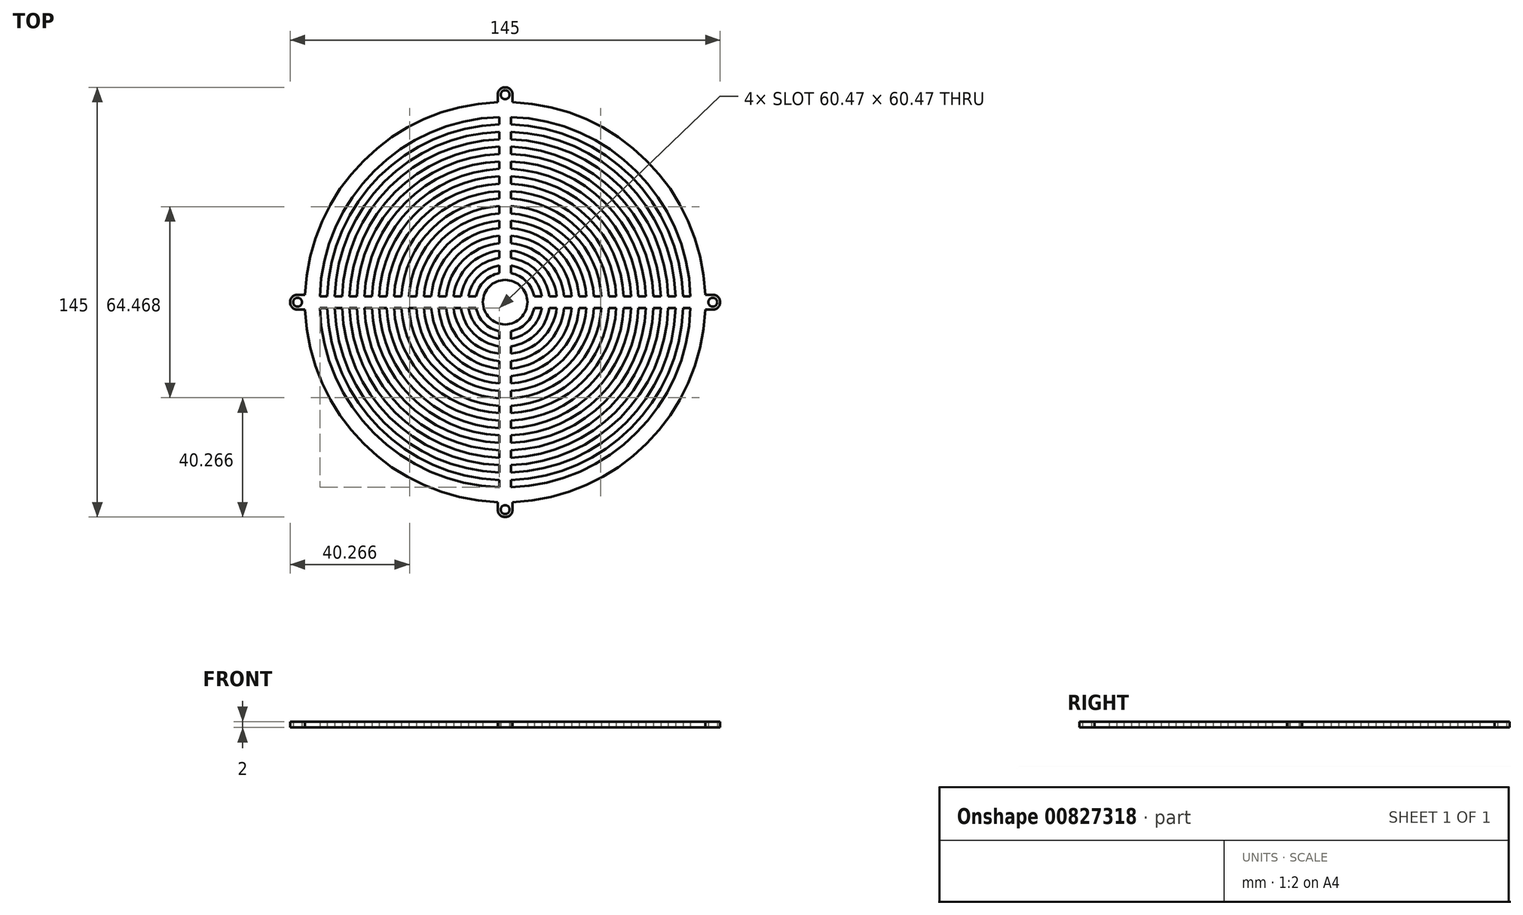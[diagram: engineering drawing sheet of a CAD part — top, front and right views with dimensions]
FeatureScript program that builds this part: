
annotation { "Feature Type Name" : "Feature", "Feature Type Description" : "" }
export const myFeature = defineFeature(function(context is Context, id is Id, definition is map)
    precondition{}
    {
        {
            var Q0;
            Q0=qCreatedBy(makeId("Top.planeOp"),FACE);
            var sketch = newSketch(context, id + "F0", { "sketchPlane" : qUnion([Q0])});
            skArc(sketch, "E0", {"start": v(-62.47, -2) * mm, "mid": v(-44.2, -44.2) * mm, "end": v(-2, -62.47) * mm});
            skArc(sketch, "E1", {"start": v(-2.5, 67.45) * mm, "mid": v(-47.73, 47.73) * mm, "end": v(-67.45, 2.5) * mm});
            skArc(sketch, "E2", {"start": v(-59.97, -2) * mm, "mid": v(-42.43, -42.43) * mm, "end": v(-2, -59.97) * mm});
            skArc(sketch, "E3", {"start": v(-57.47, -2) * mm, "mid": v(-40.66, -40.66) * mm, "end": v(-2, -57.47) * mm});
            skArc(sketch, "E4", {"start": v(-54.96, -2) * mm, "mid": v(-38.9, -38.9) * mm, "end": v(-2, -54.96) * mm});
            skArc(sketch, "E5", {"start": v(-52.46, -2) * mm, "mid": v(-37.12, -37.12) * mm, "end": v(-2, -52.46) * mm});
            skArc(sketch, "E6", {"start": v(-49.96, -2) * mm, "mid": v(-35.36, -35.36) * mm, "end": v(-2, -49.96) * mm});
            skArc(sketch, "E7", {"start": v(-47.46, -2) * mm, "mid": v(-33.59, -33.59) * mm, "end": v(-2, -47.46) * mm});
            skArc(sketch, "E8", {"start": v(-44.96, -2) * mm, "mid": v(-31.82, -31.82) * mm, "end": v(-2, -44.96) * mm});
            skArc(sketch, "E9", {"start": v(-42.45, -2) * mm, "mid": v(-30.05, -30.05) * mm, "end": v(-2, -42.45) * mm});
            skArc(sketch, "E10", {"start": v(-37.45, -2) * mm, "mid": v(-26.52, -26.52) * mm, "end": v(-2, -37.45) * mm});
            skArc(sketch, "E11", {"start": v(-39.95, -2) * mm, "mid": v(-28.28, -28.28) * mm, "end": v(-2, -39.95) * mm});
            skArc(sketch, "E12", {"start": v(-32.44, -2) * mm, "mid": v(-22.98, -22.98) * mm, "end": v(-2, -32.44) * mm});
            skArc(sketch, "E13", {"start": v(-34.94, -2) * mm, "mid": v(-24.75, -24.75) * mm, "end": v(-2, -34.94) * mm});
            skArc(sketch, "E14", {"start": v(-29.93, -2) * mm, "mid": v(-21.21, -21.21) * mm, "end": v(-2, -29.93) * mm});
            skArc(sketch, "E15", {"start": v(-27.43, -2) * mm, "mid": v(-19.45, -19.45) * mm, "end": v(-2, -27.43) * mm});
            skArc(sketch, "E16", {"start": v(-22.41, -2) * mm, "mid": v(-15.9, -15.9) * mm, "end": v(-2, -22.41) * mm});
            skArc(sketch, "E17", {"start": v(-19.9, -2) * mm, "mid": v(-14.14, -14.14) * mm, "end": v(-2, -19.9) * mm});
            skArc(sketch, "E18", {"start": v(-17.39, -2) * mm, "mid": v(-12.37, -12.37) * mm, "end": v(-2, -17.39) * mm});
            skArc(sketch, "E19", {"start": v(-9.8, -2) * mm, "mid": v(-7.07, -7.07) * mm, "end": v(-2, -9.8) * mm});
            skArc(sketch, "E20", {"start": v(-12.34, -2) * mm, "mid": v(-8.84, -8.84) * mm, "end": v(-2, -12.34) * mm});
            skArc(sketch, "E21", {"start": v(-14.87, -2) * mm, "mid": v(-10.6, -10.6) * mm, "end": v(-2, -14.87) * mm});
            skArc(sketch, "E22", {"start": v(-24.92, -2) * mm, "mid": v(-17.68, -17.68) * mm, "end": v(-2, -24.92) * mm});
            skLineSegment(sketch, "E23", {"start": v(-2, 62.47) * mm, "end": v(-2, 59.97) * mm});
            skLineSegment(sketch, "E24", {"start": v(2, 62.47) * mm, "end": v(2, 59.97) * mm});
            skLineSegment(sketch, "E25", {"start": v(-62.47, -2) * mm, "end": v(-59.97, -2) * mm});
            skLineSegment(sketch, "E26", {"start": v(-62.47, 2) * mm, "end": v(-59.97, 2) * mm});
            skLineSegment(sketch, "E27.trimOffspring", {"start": v(-57.47, 2) * mm, "end": v(-54.96, 2) * mm});
            skLineSegment(sketch, "E28.trimOffspring", {"start": v(-52.46, 2) * mm, "end": v(-49.96, 2) * mm});
            skLineSegment(sketch, "E29.trimOffspring", {"start": v(-57.47, -2) * mm, "end": v(-54.96, -2) * mm});
            skLineSegment(sketch, "E30.trimOffspring", {"start": v(-52.46, -2) * mm, "end": v(-49.96, -2) * mm});
            skLineSegment(sketch, "E31.trimOffspring", {"start": v(-47.46, -2) * mm, "end": v(-44.96, -2) * mm});
            skLineSegment(sketch, "E32.trimOffspring", {"start": v(-47.46, 2) * mm, "end": v(-44.96, 2) * mm});
            skLineSegment(sketch, "E33.trimOffspring", {"start": v(-42.45, 2) * mm, "end": v(-39.95, 2) * mm});
            skLineSegment(sketch, "E34.trimOffspring", {"start": v(-42.45, -2) * mm, "end": v(-39.95, -2) * mm});
            skLineSegment(sketch, "E35.trimOffspring", {"start": v(-37.45, 2) * mm, "end": v(-34.94, 2) * mm});
            skLineSegment(sketch, "E36.trimOffspring", {"start": v(-37.45, -2) * mm, "end": v(-34.94, -2) * mm});
            skLineSegment(sketch, "E37.trimOffspring", {"start": v(-32.44, 2) * mm, "end": v(-29.93, 2) * mm});
            skLineSegment(sketch, "E38.trimOffspring", {"start": v(-32.44, -2) * mm, "end": v(-29.93, -2) * mm});
            skLineSegment(sketch, "E39.trimOffspring", {"start": v(-27.43, 2) * mm, "end": v(-24.92, 2) * mm});
            skLineSegment(sketch, "E40.trimOffspring", {"start": v(-27.43, -2) * mm, "end": v(-24.92, -2) * mm});
            skLineSegment(sketch, "E41.trimOffspring", {"start": v(-22.41, 2) * mm, "end": v(-19.9, 2) * mm});
            skLineSegment(sketch, "E42.trimOffspring", {"start": v(-22.41, -2) * mm, "end": v(-19.9, -2) * mm});
            skLineSegment(sketch, "E43.trimOffspring", {"start": v(-17.39, 2) * mm, "end": v(-14.87, 2) * mm});
            skLineSegment(sketch, "E44.trimOffspring", {"start": v(-17.39, -2) * mm, "end": v(-14.87, -2) * mm});
            skLineSegment(sketch, "E45.trimOffspring", {"start": v(-12.34, 2) * mm, "end": v(-9.8, 2) * mm});
            skLineSegment(sketch, "E46.trimOffspring", {"start": v(-12.34, -2) * mm, "end": v(-9.8, -2) * mm});
            skLineSegment(sketch, "E47.trimOffspring", {"start": v(-2, -9.8) * mm, "end": v(-2, -12.34) * mm});
            skLineSegment(sketch, "E48.trimOffspring", {"start": v(2, -9.8) * mm, "end": v(2, -12.34) * mm});
            skLineSegment(sketch, "E49.trimOffspring", {"start": v(-2, 12.34) * mm, "end": v(-2, 9.8) * mm});
            skLineSegment(sketch, "E50.trimOffspring", {"start": v(2, 12.34) * mm, "end": v(2, 9.8) * mm});
            skLineSegment(sketch, "E51.trimOffspring", {"start": v(2, 17.39) * mm, "end": v(2, 14.87) * mm});
            skLineSegment(sketch, "E52.trimOffspring", {"start": v(-2, 17.39) * mm, "end": v(-2, 14.87) * mm});
            skArc(sketch, "E53.trimOffspring", {"start": v(-2, 12.34) * mm, "mid": v(-8.84, 8.84) * mm, "end": v(-12.34, 2) * mm});
            skArc(sketch, "E54.trimOffspring", {"start": v(-2, 9.8) * mm, "mid": v(-7.07, 7.07) * mm, "end": v(-9.8, 2) * mm});
            skArc(sketch, "E55.trimOffspring", {"start": v(-2, 14.87) * mm, "mid": v(-10.6, 10.6) * mm, "end": v(-14.87, 2) * mm});
            skArc(sketch, "E56.trimOffspring", {"start": v(-2, 17.39) * mm, "mid": v(-12.37, 12.37) * mm, "end": v(-17.39, 2) * mm});
            skArc(sketch, "E57.trimOffspring", {"start": v(-2, 19.9) * mm, "mid": v(-14.14, 14.14) * mm, "end": v(-19.9, 2) * mm});
            skArc(sketch, "E58.trimOffspring", {"start": v(-2, 22.41) * mm, "mid": v(-15.9, 15.9) * mm, "end": v(-22.41, 2) * mm});
            skArc(sketch, "E59.trimOffspring", {"start": v(-2, 24.92) * mm, "mid": v(-17.68, 17.68) * mm, "end": v(-24.92, 2) * mm});
            skArc(sketch, "E60.trimOffspring", {"start": v(-2, 27.43) * mm, "mid": v(-19.45, 19.45) * mm, "end": v(-27.43, 2) * mm});
            skArc(sketch, "E61.trimOffspring", {"start": v(-2, 29.93) * mm, "mid": v(-21.21, 21.21) * mm, "end": v(-29.93, 2) * mm});
            skArc(sketch, "E62.trimOffspring", {"start": v(-2, 32.44) * mm, "mid": v(-22.98, 22.98) * mm, "end": v(-32.44, 2) * mm});
            skLineSegment(sketch, "E63.trimOffspring", {"start": v(-2, 22.41) * mm, "end": v(-2, 19.9) * mm});
            skLineSegment(sketch, "E64.trimOffspring", {"start": v(2, 22.41) * mm, "end": v(2, 19.9) * mm});
            skLineSegment(sketch, "E65.trimOffspring", {"start": v(2, 27.43) * mm, "end": v(2, 24.92) * mm});
            skLineSegment(sketch, "E66.trimOffspring", {"start": v(-2, 27.43) * mm, "end": v(-2, 24.92) * mm});
            skLineSegment(sketch, "E67.trimOffspring", {"start": v(-2, 32.44) * mm, "end": v(-2, 29.93) * mm});
            skLineSegment(sketch, "E68.trimOffspring", {"start": v(2, 32.44) * mm, "end": v(2, 29.93) * mm});
            skArc(sketch, "E69.trimOffspring", {"start": v(-2, 34.94) * mm, "mid": v(-24.75, 24.75) * mm, "end": v(-34.94, 2) * mm});
            skArc(sketch, "E70.trimOffspring", {"start": v(-2, 37.45) * mm, "mid": v(-26.52, 26.52) * mm, "end": v(-37.45, 2) * mm});
            skArc(sketch, "E71.trimOffspring", {"start": v(-2, 39.95) * mm, "mid": v(-28.28, 28.28) * mm, "end": v(-39.95, 2) * mm});
            skArc(sketch, "E72.trimOffspring", {"start": v(-2, 42.45) * mm, "mid": v(-30.05, 30.05) * mm, "end": v(-42.45, 2) * mm});
            skArc(sketch, "E73.trimOffspring", {"start": v(-2, 44.96) * mm, "mid": v(-31.82, 31.82) * mm, "end": v(-44.96, 2) * mm});
            skArc(sketch, "E74.trimOffspring", {"start": v(-2, 47.46) * mm, "mid": v(-33.59, 33.59) * mm, "end": v(-47.46, 2) * mm});
            skLineSegment(sketch, "E75.trimOffspring", {"start": v(-2, 37.45) * mm, "end": v(-2, 34.94) * mm});
            skLineSegment(sketch, "E76.trimOffspring", {"start": v(2, 37.45) * mm, "end": v(2, 34.94) * mm});
            skLineSegment(sketch, "E77.trimOffspring", {"start": v(2, 42.45) * mm, "end": v(2, 39.95) * mm});
            skLineSegment(sketch, "E78.trimOffspring", {"start": v(-2, 42.45) * mm, "end": v(-2, 39.95) * mm});
            skLineSegment(sketch, "E79.trimOffspring", {"start": v(-2, 47.46) * mm, "end": v(-2, 44.96) * mm});
            skArc(sketch, "E80.trimOffspring", {"start": v(-2, 49.96) * mm, "mid": v(-35.36, 35.36) * mm, "end": v(-49.96, 2) * mm});
            skLineSegment(sketch, "E81.trimOffspring", {"start": v(2, 47.46) * mm, "end": v(2, 44.96) * mm});
            skArc(sketch, "E82.trimOffspring", {"start": v(-2, 52.46) * mm, "mid": v(-37.12, 37.12) * mm, "end": v(-52.46, 2) * mm});
            skArc(sketch, "E83.trimOffspring", {"start": v(-2, 54.96) * mm, "mid": v(-38.9, 38.9) * mm, "end": v(-54.96, 2) * mm});
            skArc(sketch, "E84.trimOffspring", {"start": v(-2, 57.47) * mm, "mid": v(-40.66, 40.66) * mm, "end": v(-57.47, 2) * mm});
            skArc(sketch, "E85.trimOffspring", {"start": v(-2, 59.97) * mm, "mid": v(-42.43, 42.43) * mm, "end": v(-59.97, 2) * mm});
            skLineSegment(sketch, "E86.trimOffspring", {"start": v(-2, 52.46) * mm, "end": v(-2, 49.96) * mm});
            skLineSegment(sketch, "E87.trimOffspring", {"start": v(2, 52.46) * mm, "end": v(2, 49.96) * mm});
            skLineSegment(sketch, "E88.trimOffspring", {"start": v(2, 57.47) * mm, "end": v(2, 54.96) * mm});
            skLineSegment(sketch, "E89.trimOffspring", {"start": v(-2, 57.47) * mm, "end": v(-2, 54.96) * mm});
            skArc(sketch, "E90.trimOffspring", {"start": v(-2, 62.47) * mm, "mid": v(-44.2, 44.2) * mm, "end": v(-62.47, 2) * mm});
            skArc(sketch, "E91.trimOffspring", {"start": v(2, -9.8) * mm, "mid": v(7.07, -7.07) * mm, "end": v(9.8, -2) * mm});
            skArc(sketch, "E92.trimOffspring", {"start": v(2, -12.34) * mm, "mid": v(8.84, -8.84) * mm, "end": v(12.34, -2) * mm});
            skArc(sketch, "E93.trimOffspring", {"start": v(2, -14.87) * mm, "mid": v(10.6, -10.6) * mm, "end": v(14.87, -2) * mm});
            skArc(sketch, "E94.trimOffspring", {"start": v(2, -17.39) * mm, "mid": v(12.37, -12.37) * mm, "end": v(17.39, -2) * mm});
            skArc(sketch, "E95.trimOffspring", {"start": v(2, -19.9) * mm, "mid": v(14.14, -14.14) * mm, "end": v(19.9, -2) * mm});
            skArc(sketch, "E96.trimOffspring", {"start": v(2, -22.41) * mm, "mid": v(15.9, -15.9) * mm, "end": v(22.41, -2) * mm});
            skArc(sketch, "E97.trimOffspring", {"start": v(2, -24.92) * mm, "mid": v(17.68, -17.68) * mm, "end": v(24.92, -2) * mm});
            skArc(sketch, "E98.trimOffspring", {"start": v(2, -27.43) * mm, "mid": v(19.45, -19.45) * mm, "end": v(27.43, -2) * mm});
            skArc(sketch, "E99.trimOffspring", {"start": v(2, -29.93) * mm, "mid": v(21.21, -21.21) * mm, "end": v(29.93, -2) * mm});
            skArc(sketch, "E100.trimOffspring", {"start": v(2, -32.44) * mm, "mid": v(22.98, -22.98) * mm, "end": v(32.44, -2) * mm});
            skArc(sketch, "E101.trimOffspring", {"start": v(2, -34.94) * mm, "mid": v(24.75, -24.75) * mm, "end": v(34.94, -2) * mm});
            skArc(sketch, "E102.trimOffspring", {"start": v(2, -37.45) * mm, "mid": v(26.52, -26.52) * mm, "end": v(37.45, -2) * mm});
            skArc(sketch, "E103.trimOffspring", {"start": v(2, -39.95) * mm, "mid": v(28.28, -28.28) * mm, "end": v(39.95, -2) * mm});
            skArc(sketch, "E104.trimOffspring", {"start": v(2, -42.45) * mm, "mid": v(30.05, -30.05) * mm, "end": v(42.45, -2) * mm});
            skLineSegment(sketch, "E105.trimOffspring", {"start": v(-2, -14.87) * mm, "end": v(-2, -17.39) * mm});
            skLineSegment(sketch, "E106.trimOffspring", {"start": v(-2, -19.9) * mm, "end": v(-2, -22.41) * mm});
            skLineSegment(sketch, "E107.trimOffspring", {"start": v(2, -19.9) * mm, "end": v(2, -22.41) * mm});
            skLineSegment(sketch, "E108", {"start": v(2, -14.87) * mm, "end": v(2, -17.39) * mm});
            skLineSegment(sketch, "E109.trimOffspring", {"start": v(2, -29.93) * mm, "end": v(2, -32.44) * mm});
            skLineSegment(sketch, "E110.trimOffspring", {"start": v(-2, -29.93) * mm, "end": v(-2, -32.44) * mm});
            skLineSegment(sketch, "E111", {"start": v(2, -27.43) * mm, "end": v(2, -24.92) * mm});
            skLineSegment(sketch, "E112", {"start": v(-2, -27.43) * mm, "end": v(-2, -24.92) * mm});
            skLineSegment(sketch, "E113.trimOffspring", {"start": v(-2, -34.94) * mm, "end": v(-2, -37.45) * mm});
            skLineSegment(sketch, "E114.trimOffspring", {"start": v(-2, -39.95) * mm, "end": v(-2, -42.45) * mm});
            skLineSegment(sketch, "E115.trimOffspring", {"start": v(2, -39.95) * mm, "end": v(2, -42.45) * mm});
            skLineSegment(sketch, "E116.trimOffspring", {"start": v(-2, -44.96) * mm, "end": v(-2, -47.46) * mm});
            skArc(sketch, "E117.trimOffspring", {"start": v(2, -44.96) * mm, "mid": v(31.82, -31.82) * mm, "end": v(44.96, -2) * mm});
            skArc(sketch, "E118.trimOffspring", {"start": v(2, -47.46) * mm, "mid": v(33.59, -33.59) * mm, "end": v(47.46, -2) * mm});
            skArc(sketch, "E119.trimOffspring", {"start": v(2, -49.96) * mm, "mid": v(35.36, -35.36) * mm, "end": v(49.96, -2) * mm});
            skArc(sketch, "E120.trimOffspring", {"start": v(2, -52.46) * mm, "mid": v(37.12, -37.12) * mm, "end": v(52.46, -2) * mm});
            skArc(sketch, "E121.trimOffspring", {"start": v(2, -57.47) * mm, "mid": v(40.66, -40.66) * mm, "end": v(57.47, -2) * mm});
            skArc(sketch, "E122.trimOffspring", {"start": v(2, -54.96) * mm, "mid": v(38.9, -38.9) * mm, "end": v(54.96, -2) * mm});
            skLineSegment(sketch, "E123.trimOffspring", {"start": v(-2, -49.96) * mm, "end": v(-2, -52.46) * mm});
            skLineSegment(sketch, "E124.trimOffspring", {"start": v(2, -49.96) * mm, "end": v(2, -52.46) * mm});
            skLineSegment(sketch, "E125.trimOffspring", {"start": v(2, -44.96) * mm, "end": v(2, -47.46) * mm});
            skLineSegment(sketch, "E126", {"start": v(2, -37.45) * mm, "end": v(2, -34.94) * mm});
            skLineSegment(sketch, "E127.trimOffspring", {"start": v(-2, -54.96) * mm, "end": v(-2, -57.47) * mm});
            skLineSegment(sketch, "E128.trimOffspring", {"start": v(2, -54.96) * mm, "end": v(2, -57.47) * mm});
            skArc(sketch, "E129.trimOffspring", {"start": v(2, -59.97) * mm, "mid": v(42.43, -42.43) * mm, "end": v(59.97, -2) * mm});
            skArc(sketch, "E130.trimOffspring", {"start": v(2, -62.47) * mm, "mid": v(44.2, -44.2) * mm, "end": v(62.47, -2) * mm});
            skLineSegment(sketch, "E131.trimOffspring", {"start": v(-2, -59.97) * mm, "end": v(-2, -62.47) * mm});
            skLineSegment(sketch, "E132.trimOffspring", {"start": v(2, -59.97) * mm, "end": v(2, -62.47) * mm});
            skArc(sketch, "E133.trimOffspring", {"start": v(9.8, 2) * mm, "mid": v(7.07, 7.07) * mm, "end": v(2, 9.8) * mm});
            skArc(sketch, "E134.trimOffspring", {"start": v(12.34, 2) * mm, "mid": v(8.84, 8.84) * mm, "end": v(2, 12.34) * mm});
            skArc(sketch, "E135.trimOffspring", {"start": v(14.87, 2) * mm, "mid": v(10.6, 10.6) * mm, "end": v(2, 14.87) * mm});
            skArc(sketch, "E136.trimOffspring", {"start": v(17.39, 2) * mm, "mid": v(12.37, 12.37) * mm, "end": v(2, 17.39) * mm});
            skArc(sketch, "E137.trimOffspring", {"start": v(19.9, 2) * mm, "mid": v(14.14, 14.14) * mm, "end": v(2, 19.9) * mm});
            skArc(sketch, "E138.trimOffspring", {"start": v(22.41, 2) * mm, "mid": v(15.9, 15.9) * mm, "end": v(2, 22.41) * mm});
            skArc(sketch, "E139.trimOffspring", {"start": v(24.92, 2) * mm, "mid": v(17.68, 17.68) * mm, "end": v(2, 24.92) * mm});
            skArc(sketch, "E140.trimOffspring", {"start": v(27.43, 2) * mm, "mid": v(19.45, 19.45) * mm, "end": v(2, 27.43) * mm});
            skArc(sketch, "E141.trimOffspring", {"start": v(29.93, 2) * mm, "mid": v(21.21, 21.21) * mm, "end": v(2, 29.93) * mm});
            skArc(sketch, "E142.trimOffspring", {"start": v(32.44, 2) * mm, "mid": v(22.98, 22.98) * mm, "end": v(2, 32.44) * mm});
            skArc(sketch, "E143.trimOffspring", {"start": v(34.94, 2) * mm, "mid": v(24.75, 24.75) * mm, "end": v(2, 34.94) * mm});
            skArc(sketch, "E144.trimOffspring", {"start": v(37.45, 2) * mm, "mid": v(26.52, 26.52) * mm, "end": v(2, 37.45) * mm});
            skArc(sketch, "E145.trimOffspring", {"start": v(39.95, 2) * mm, "mid": v(28.28, 28.28) * mm, "end": v(2, 39.95) * mm});
            skArc(sketch, "E146.trimOffspring", {"start": v(42.45, 2) * mm, "mid": v(30.05, 30.05) * mm, "end": v(2, 42.45) * mm});
            skArc(sketch, "E147.trimOffspring", {"start": v(44.96, 2) * mm, "mid": v(31.82, 31.82) * mm, "end": v(2, 44.96) * mm});
            skArc(sketch, "E148.trimOffspring", {"start": v(47.46, 2) * mm, "mid": v(33.59, 33.59) * mm, "end": v(2, 47.46) * mm});
            skArc(sketch, "E149.trimOffspring", {"start": v(49.96, 2) * mm, "mid": v(35.36, 35.36) * mm, "end": v(2, 49.96) * mm});
            skArc(sketch, "E150.trimOffspring", {"start": v(52.46, 2) * mm, "mid": v(37.12, 37.12) * mm, "end": v(2, 52.46) * mm});
            skArc(sketch, "E151.trimOffspring", {"start": v(54.96, 2) * mm, "mid": v(38.9, 38.9) * mm, "end": v(2, 54.96) * mm});
            skArc(sketch, "E152.trimOffspring", {"start": v(57.47, 2) * mm, "mid": v(40.66, 40.66) * mm, "end": v(2, 57.47) * mm});
            skArc(sketch, "E153.trimOffspring", {"start": v(59.97, 2) * mm, "mid": v(42.43, 42.43) * mm, "end": v(2, 59.97) * mm});
            skArc(sketch, "E154.trimOffspring", {"start": v(62.47, 2) * mm, "mid": v(44.2, 44.2) * mm, "end": v(2, 62.47) * mm});
            skLineSegment(sketch, "E155.trimOffspring", {"start": v(24.92, 2) * mm, "end": v(27.43, 2) * mm});
            skLineSegment(sketch, "E156.trimOffspring", {"start": v(14.87, -2) * mm, "end": v(17.39, -2) * mm});
            skLineSegment(sketch, "E157.trimOffspring", {"start": v(24.92, -2) * mm, "end": v(27.43, -2) * mm});
            skLineSegment(sketch, "E158.trimOffspring", {"start": v(34.94, -2) * mm, "end": v(37.45, -2) * mm});
            skLineSegment(sketch, "E159", {"start": v(9.8, 2) * mm, "end": v(12.34, 2) * mm});
            skLineSegment(sketch, "E160", {"start": v(9.8, -2) * mm, "end": v(12.34, -2) * mm});
            skLineSegment(sketch, "E161", {"start": v(14.87, 2) * mm, "end": v(17.39, 2) * mm});
            skLineSegment(sketch, "E162", {"start": v(19.9, -2) * mm, "end": v(22.41, -2) * mm});
            skLineSegment(sketch, "E163", {"start": v(19.9, 2) * mm, "end": v(22.41, 2) * mm});
            skLineSegment(sketch, "E164.trimOffspring", {"start": v(29.93, 2) * mm, "end": v(32.44, 2) * mm});
            skLineSegment(sketch, "E165", {"start": v(29.93, -2) * mm, "end": v(32.44, -2) * mm});
            skLineSegment(sketch, "E166.trimOffspring", {"start": v(39.95, -2) * mm, "end": v(42.45, -2) * mm});
            skLineSegment(sketch, "E167.trimOffspring", {"start": v(39.95, 2) * mm, "end": v(42.45, 2) * mm});
            skLineSegment(sketch, "E168.trimOffspring", {"start": v(44.96, -2) * mm, "end": v(47.46, -2) * mm});
            skLineSegment(sketch, "E169.trimOffspring", {"start": v(49.96, -2) * mm, "end": v(52.46, -2) * mm});
            skLineSegment(sketch, "E170.trimOffspring", {"start": v(49.96, 2) * mm, "end": v(52.46, 2) * mm});
            skLineSegment(sketch, "E171.trimOffspring", {"start": v(54.96, 2) * mm, "end": v(57.47, 2) * mm});
            skLineSegment(sketch, "E172", {"start": v(34.94, 2) * mm, "end": v(37.45, 2) * mm});
            skLineSegment(sketch, "E173", {"start": v(44.96, 2) * mm, "end": v(47.46, 2) * mm});
            skLineSegment(sketch, "E174.trimOffspring", {"start": v(54.96, -2) * mm, "end": v(57.47, -2) * mm});
            skLineSegment(sketch, "E175.trimOffspring", {"start": v(59.97, 2) * mm, "end": v(62.47, 2) * mm});
            skLineSegment(sketch, "E176.trimOffspring", {"start": v(59.97, -2) * mm, "end": v(62.47, -2) * mm});
            skCircle(sketch, "E177", {"center": v(0, 0) * mm, "radius": 7.5 * mm});
            skArc(sketch, "E178", {"start": v(2.5, 70) * mm, "mid": v(0, 72.5) * mm, "end": v(-2.5, 70) * mm});
            skLineSegment(sketch, "E179", {"start": v(-2.5, 70) * mm, "end": v(-2.5, 67.45) * mm});
            skLineSegment(sketch, "E180", {"start": v(2.5, 70) * mm, "end": v(2.5, 67.45) * mm});
            skLineSegment(sketch, "E181.MirrorCS", {"start": v(2, -62.47) * mm, "end": v(2, -59.97) * mm});
            skLineSegment(sketch, "E182.MirrorCS", {"start": v(-2.5, -70) * mm, "end": v(-2.5, -67.45) * mm});
            skLineSegment(sketch, "E183.MirrorCS", {"start": v(2.5, -70) * mm, "end": v(2.5, -67.45) * mm});
            skLineSegment(sketch, "E184.MirrorCS", {"start": v(-2, -62.47) * mm, "end": v(-2, -59.97) * mm});
            skLineSegment(sketch, "E185.MirrorCS", {"start": v(-2, -57.47) * mm, "end": v(-2, -54.96) * mm});
            skLineSegment(sketch, "E186.MirrorCS", {"start": v(2, -57.47) * mm, "end": v(2, -54.96) * mm});
            skArc(sketch, "E187.MirrorCS", {"start": v(2.5, -70) * mm, "mid": v(0, -72.5) * mm, "end": v(-2.5, -70) * mm});
            skArc(sketch, "E188", {"start": v(-70, 2.5) * mm, "mid": v(-72.5, 0) * mm, "end": v(-70, -2.5) * mm});
            skLineSegment(sketch, "E189", {"start": v(-70, 2.5) * mm, "end": v(-67.45, 2.5) * mm});
            skLineSegment(sketch, "E190", {"start": v(-70, -2.5) * mm, "end": v(-67.45, -2.5) * mm});
            skArc(sketch, "E191.trimOffspring", {"start": v(-67.45, -2.5) * mm, "mid": v(-47.73, -47.73) * mm, "end": v(-2.5, -67.45) * mm});
            skArc(sketch, "E192.MirrorCS", {"start": v(70, 2.5) * mm, "mid": v(72.5, 0) * mm, "end": v(70, -2.5) * mm});
            skLineSegment(sketch, "E193.MirrorCS", {"start": v(70, 2.5) * mm, "end": v(67.45, 2.5) * mm});
            skLineSegment(sketch, "E194.MirrorCS", {"start": v(70, -2.5) * mm, "end": v(67.45, -2.5) * mm});
            skArc(sketch, "E195.trimOffspring", {"start": v(2.5, -67.45) * mm, "mid": v(47.73, -47.73) * mm, "end": v(67.45, -2.5) * mm});
            skArc(sketch, "E196.trimOffspring", {"start": v(67.45, 2.5) * mm, "mid": v(47.73, 47.73) * mm, "end": v(2.5, 67.45) * mm});
            skSolve(sketch);
        }
        {
            var Q0;
            Q0 = qSketchRegion(id + "F0", true);
            var Q1;
            {var subQ24=sQuery(id+"F0.wireOp",EDGE,"E41.trimOffspring");Q1=makeQuery(id+"F0.imprint","IMPRINT",FACE,{"disambiguationData":[TD([[makeQuery(id+"F0.imprint","IMPRINT",EDGE,{"derivedFrom":subQ24}),-1.0]])]});}
            extrude(context, id + "F1", {"entities" : qUnion([Q0, Q1]), "depth" : 2 * mm, "offsetDistance" : 25 * mm});
        }
        {
            var Q0;
            Q0=sQuery(id+"F0.wireOp",VERTEX,"E187.MirrorCS.center");
            var Q1;
            Q1=sQuery(id+"F0.wireOp",VERTEX,"E192.MirrorCS.center");
            var Q2;
            Q2=sQuery(id+"F0.wireOp",VERTEX,"E178.center");
            var Q3;
            Q3=sQuery(id+"F0.wireOp",VERTEX,"E188.center");
            var Q4;
            Q4=makeQuery(id+"F1.opExtrude","SWEPT_BODY",BODY,{"disambiguationData":[OSD([sQuery(id+"F0.wireOp",EDGE,"E0"),sQuery(id+"F0.wireOp",EDGE,"E1"),sQuery(id+"F0.wireOp",EDGE,"E2"),sQuery(id+"F0.wireOp",EDGE,"E3"),sQuery(id+"F0.wireOp",EDGE,"E4"),sQuery(id+"F0.wireOp",EDGE,"E5"),sQuery(id+"F0.wireOp",EDGE,"E6"),sQuery(id+"F0.wireOp",EDGE,"E7"),sQuery(id+"F0.wireOp",EDGE,"E8"),sQuery(id+"F0.wireOp",EDGE,"E9"),sQuery(id+"F0.wireOp",EDGE,"E10"),sQuery(id+"F0.wireOp",EDGE,"E11"),sQuery(id+"F0.wireOp",EDGE,"E12"),sQuery(id+"F0.wireOp",EDGE,"E13"),sQuery(id+"F0.wireOp",EDGE,"E14"),sQuery(id+"F0.wireOp",EDGE,"E15"),sQuery(id+"F0.wireOp",EDGE,"E16"),sQuery(id+"F0.wireOp",EDGE,"E17"),sQuery(id+"F0.wireOp",EDGE,"E18"),sQuery(id+"F0.wireOp",EDGE,"E19"),sQuery(id+"F0.wireOp",EDGE,"E20"),sQuery(id+"F0.wireOp",EDGE,"E21"),sQuery(id+"F0.wireOp",EDGE,"E22"),sQuery(id+"F0.wireOp",EDGE,"E23"),sQuery(id+"F0.wireOp",EDGE,"E24"),sQuery(id+"F0.wireOp",EDGE,"E25"),sQuery(id+"F0.wireOp",EDGE,"E26"),sQuery(id+"F0.wireOp",EDGE,"E27.trimOffspring"),sQuery(id+"F0.wireOp",EDGE,"E28.trimOffspring"),sQuery(id+"F0.wireOp",EDGE,"E29.trimOffspring"),sQuery(id+"F0.wireOp",EDGE,"E30.trimOffspring"),sQuery(id+"F0.wireOp",EDGE,"E31.trimOffspring"),sQuery(id+"F0.wireOp",EDGE,"E32.trimOffspring"),sQuery(id+"F0.wireOp",EDGE,"E33.trimOffspring"),sQuery(id+"F0.wireOp",EDGE,"E34.trimOffspring"),sQuery(id+"F0.wireOp",EDGE,"E35.trimOffspring"),sQuery(id+"F0.wireOp",EDGE,"E36.trimOffspring"),sQuery(id+"F0.wireOp",EDGE,"E37.trimOffspring"),sQuery(id+"F0.wireOp",EDGE,"E38.trimOffspring"),sQuery(id+"F0.wireOp",EDGE,"E39.trimOffspring"),sQuery(id+"F0.wireOp",EDGE,"E40.trimOffspring"),sQuery(id+"F0.wireOp",EDGE,"E41.trimOffspring"),sQuery(id+"F0.wireOp",EDGE,"E42.trimOffspring"),sQuery(id+"F0.wireOp",EDGE,"E43.trimOffspring"),sQuery(id+"F0.wireOp",EDGE,"E44.trimOffspring"),sQuery(id+"F0.wireOp",EDGE,"E45.trimOffspring"),sQuery(id+"F0.wireOp",EDGE,"E46.trimOffspring"),sQuery(id+"F0.wireOp",EDGE,"E47.trimOffspring"),sQuery(id+"F0.wireOp",EDGE,"E48.trimOffspring"),sQuery(id+"F0.wireOp",EDGE,"E49.trimOffspring"),sQuery(id+"F0.wireOp",EDGE,"E50.trimOffspring"),sQuery(id+"F0.wireOp",EDGE,"E51.trimOffspring"),sQuery(id+"F0.wireOp",EDGE,"E52.trimOffspring"),sQuery(id+"F0.wireOp",EDGE,"E53.trimOffspring"),sQuery(id+"F0.wireOp",EDGE,"E54.trimOffspring"),sQuery(id+"F0.wireOp",EDGE,"E55.trimOffspring"),sQuery(id+"F0.wireOp",EDGE,"E56.trimOffspring"),sQuery(id+"F0.wireOp",EDGE,"E57.trimOffspring"),sQuery(id+"F0.wireOp",EDGE,"E58.trimOffspring"),sQuery(id+"F0.wireOp",EDGE,"E59.trimOffspring"),sQuery(id+"F0.wireOp",EDGE,"E60.trimOffspring"),sQuery(id+"F0.wireOp",EDGE,"E61.trimOffspring"),sQuery(id+"F0.wireOp",EDGE,"E62.trimOffspring"),sQuery(id+"F0.wireOp",EDGE,"E63.trimOffspring"),sQuery(id+"F0.wireOp",EDGE,"E64.trimOffspring"),sQuery(id+"F0.wireOp",EDGE,"E65.trimOffspring"),sQuery(id+"F0.wireOp",EDGE,"E66.trimOffspring"),sQuery(id+"F0.wireOp",EDGE,"E67.trimOffspring"),sQuery(id+"F0.wireOp",EDGE,"E68.trimOffspring"),sQuery(id+"F0.wireOp",EDGE,"E69.trimOffspring"),sQuery(id+"F0.wireOp",EDGE,"E70.trimOffspring"),sQuery(id+"F0.wireOp",EDGE,"E71.trimOffspring"),sQuery(id+"F0.wireOp",EDGE,"E72.trimOffspring"),sQuery(id+"F0.wireOp",EDGE,"E73.trimOffspring"),sQuery(id+"F0.wireOp",EDGE,"E74.trimOffspring"),sQuery(id+"F0.wireOp",EDGE,"E75.trimOffspring"),sQuery(id+"F0.wireOp",EDGE,"E76.trimOffspring"),sQuery(id+"F0.wireOp",EDGE,"E77.trimOffspring"),sQuery(id+"F0.wireOp",EDGE,"E78.trimOffspring"),sQuery(id+"F0.wireOp",EDGE,"E79.trimOffspring"),sQuery(id+"F0.wireOp",EDGE,"E80.trimOffspring"),sQuery(id+"F0.wireOp",EDGE,"E81.trimOffspring"),sQuery(id+"F0.wireOp",EDGE,"E82.trimOffspring"),sQuery(id+"F0.wireOp",EDGE,"E83.trimOffspring"),sQuery(id+"F0.wireOp",EDGE,"E84.trimOffspring"),sQuery(id+"F0.wireOp",EDGE,"E85.trimOffspring"),sQuery(id+"F0.wireOp",EDGE,"E86.trimOffspring"),sQuery(id+"F0.wireOp",EDGE,"E87.trimOffspring"),sQuery(id+"F0.wireOp",EDGE,"E88.trimOffspring"),sQuery(id+"F0.wireOp",EDGE,"E89.trimOffspring"),sQuery(id+"F0.wireOp",EDGE,"E90.trimOffspring"),sQuery(id+"F0.wireOp",EDGE,"E91.trimOffspring"),sQuery(id+"F0.wireOp",EDGE,"E92.trimOffspring"),sQuery(id+"F0.wireOp",EDGE,"E93.trimOffspring"),sQuery(id+"F0.wireOp",EDGE,"E94.trimOffspring"),sQuery(id+"F0.wireOp",EDGE,"E95.trimOffspring"),sQuery(id+"F0.wireOp",EDGE,"E96.trimOffspring"),sQuery(id+"F0.wireOp",EDGE,"E97.trimOffspring"),sQuery(id+"F0.wireOp",EDGE,"E98.trimOffspring"),sQuery(id+"F0.wireOp",EDGE,"E99.trimOffspring"),sQuery(id+"F0.wireOp",EDGE,"E100.trimOffspring"),sQuery(id+"F0.wireOp",EDGE,"E101.trimOffspring"),sQuery(id+"F0.wireOp",EDGE,"E102.trimOffspring"),sQuery(id+"F0.wireOp",EDGE,"E103.trimOffspring"),sQuery(id+"F0.wireOp",EDGE,"E104.trimOffspring"),sQuery(id+"F0.wireOp",EDGE,"E105.trimOffspring"),sQuery(id+"F0.wireOp",EDGE,"E106.trimOffspring"),sQuery(id+"F0.wireOp",EDGE,"E107.trimOffspring"),sQuery(id+"F0.wireOp",EDGE,"E108"),sQuery(id+"F0.wireOp",EDGE,"E109.trimOffspring"),sQuery(id+"F0.wireOp",EDGE,"E110.trimOffspring"),sQuery(id+"F0.wireOp",EDGE,"E111"),sQuery(id+"F0.wireOp",EDGE,"E112"),sQuery(id+"F0.wireOp",EDGE,"E113.trimOffspring"),sQuery(id+"F0.wireOp",EDGE,"E114.trimOffspring"),sQuery(id+"F0.wireOp",EDGE,"E115.trimOffspring"),sQuery(id+"F0.wireOp",EDGE,"E116.trimOffspring"),sQuery(id+"F0.wireOp",EDGE,"E117.trimOffspring"),sQuery(id+"F0.wireOp",EDGE,"E118.trimOffspring"),sQuery(id+"F0.wireOp",EDGE,"E119.trimOffspring"),sQuery(id+"F0.wireOp",EDGE,"E120.trimOffspring"),sQuery(id+"F0.wireOp",EDGE,"E121.trimOffspring"),sQuery(id+"F0.wireOp",EDGE,"E122.trimOffspring"),sQuery(id+"F0.wireOp",EDGE,"E123.trimOffspring"),sQuery(id+"F0.wireOp",EDGE,"E124.trimOffspring"),sQuery(id+"F0.wireOp",EDGE,"E125.trimOffspring"),sQuery(id+"F0.wireOp",EDGE,"E126"),sQuery(id+"F0.wireOp",EDGE,"E129.trimOffspring"),sQuery(id+"F0.wireOp",EDGE,"E130.trimOffspring"),sQuery(id+"F0.wireOp",EDGE,"E133.trimOffspring"),sQuery(id+"F0.wireOp",EDGE,"E134.trimOffspring"),sQuery(id+"F0.wireOp",EDGE,"E135.trimOffspring"),sQuery(id+"F0.wireOp",EDGE,"E136.trimOffspring"),sQuery(id+"F0.wireOp",EDGE,"E137.trimOffspring"),sQuery(id+"F0.wireOp",EDGE,"E138.trimOffspring"),sQuery(id+"F0.wireOp",EDGE,"E139.trimOffspring"),sQuery(id+"F0.wireOp",EDGE,"E140.trimOffspring"),sQuery(id+"F0.wireOp",EDGE,"E141.trimOffspring"),sQuery(id+"F0.wireOp",EDGE,"E142.trimOffspring"),sQuery(id+"F0.wireOp",EDGE,"E143.trimOffspring"),sQuery(id+"F0.wireOp",EDGE,"E144.trimOffspring"),sQuery(id+"F0.wireOp",EDGE,"E145.trimOffspring"),sQuery(id+"F0.wireOp",EDGE,"E146.trimOffspring"),sQuery(id+"F0.wireOp",EDGE,"E147.trimOffspring"),sQuery(id+"F0.wireOp",EDGE,"E148.trimOffspring"),sQuery(id+"F0.wireOp",EDGE,"E149.trimOffspring"),sQuery(id+"F0.wireOp",EDGE,"E150.trimOffspring"),sQuery(id+"F0.wireOp",EDGE,"E151.trimOffspring"),sQuery(id+"F0.wireOp",EDGE,"E152.trimOffspring"),sQuery(id+"F0.wireOp",EDGE,"E153.trimOffspring"),sQuery(id+"F0.wireOp",EDGE,"E154.trimOffspring"),sQuery(id+"F0.wireOp",EDGE,"E155.trimOffspring"),sQuery(id+"F0.wireOp",EDGE,"E156.trimOffspring"),sQuery(id+"F0.wireOp",EDGE,"E157.trimOffspring"),sQuery(id+"F0.wireOp",EDGE,"E158.trimOffspring"),sQuery(id+"F0.wireOp",EDGE,"E159"),sQuery(id+"F0.wireOp",EDGE,"E160"),sQuery(id+"F0.wireOp",EDGE,"E161"),sQuery(id+"F0.wireOp",EDGE,"E162"),sQuery(id+"F0.wireOp",EDGE,"E163"),sQuery(id+"F0.wireOp",EDGE,"E164.trimOffspring"),sQuery(id+"F0.wireOp",EDGE,"E165"),sQuery(id+"F0.wireOp",EDGE,"E166.trimOffspring"),sQuery(id+"F0.wireOp",EDGE,"E167.trimOffspring"),sQuery(id+"F0.wireOp",EDGE,"E168.trimOffspring"),sQuery(id+"F0.wireOp",EDGE,"E169.trimOffspring"),sQuery(id+"F0.wireOp",EDGE,"E170.trimOffspring"),sQuery(id+"F0.wireOp",EDGE,"E171.trimOffspring"),sQuery(id+"F0.wireOp",EDGE,"E172"),sQuery(id+"F0.wireOp",EDGE,"E173"),sQuery(id+"F0.wireOp",EDGE,"E174.trimOffspring"),sQuery(id+"F0.wireOp",EDGE,"E175.trimOffspring"),sQuery(id+"F0.wireOp",EDGE,"E176.trimOffspring"),sQuery(id+"F0.wireOp",EDGE,"E177"),sQuery(id+"F0.wireOp",EDGE,"E178"),sQuery(id+"F0.wireOp",EDGE,"E179"),sQuery(id+"F0.wireOp",EDGE,"E180"),sQuery(id+"F0.wireOp",EDGE,"E181.MirrorCS"),sQuery(id+"F0.wireOp",EDGE,"E182.MirrorCS"),sQuery(id+"F0.wireOp",EDGE,"E183.MirrorCS"),sQuery(id+"F0.wireOp",EDGE,"E184.MirrorCS"),sQuery(id+"F0.wireOp",EDGE,"E185.MirrorCS"),sQuery(id+"F0.wireOp",EDGE,"E186.MirrorCS"),sQuery(id+"F0.wireOp",EDGE,"E187.MirrorCS"),sQuery(id+"F0.wireOp",EDGE,"E188"),sQuery(id+"F0.wireOp",EDGE,"E189"),sQuery(id+"F0.wireOp",EDGE,"E190"),sQuery(id+"F0.wireOp",EDGE,"E191.trimOffspring"),sQuery(id+"F0.wireOp",EDGE,"E192.MirrorCS"),sQuery(id+"F0.wireOp",EDGE,"E193.MirrorCS"),sQuery(id+"F0.wireOp",EDGE,"E194.MirrorCS"),sQuery(id+"F0.wireOp",EDGE,"E195.trimOffspring"),sQuery(id+"F0.wireOp",EDGE,"E196.trimOffspring")])]});
            hole(context, id + "F2", {"style" : HoleStyle.SIMPLE, "endStyle" : HoleEndStyle.BLIND, "oppositeDirection" : true, "holeDiameter" : 3 * mm, "majorDiameter" : 5 * mm, "holeDepth" : 4.5 * mm, "isTappedThrough" : true, "tappedDepth" : 12 * mm, "tapClearance" : 3, "startFromSketch" : true, "locations" : qUnion([Q0, Q1, Q2, Q3]), "scope" : qUnion([Q4])});
        }
    });
